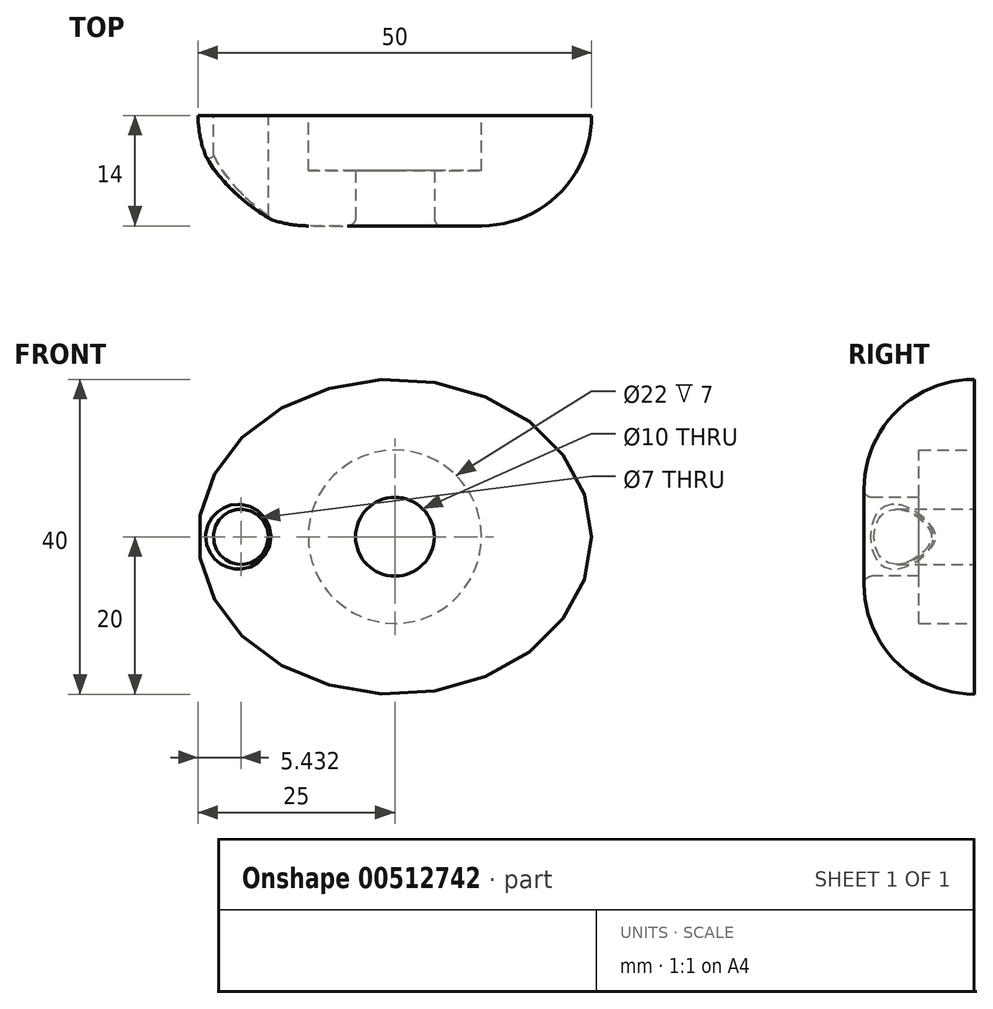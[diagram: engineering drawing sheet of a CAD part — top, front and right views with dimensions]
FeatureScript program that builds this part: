
annotation { "Feature Type Name" : "Feature", "Feature Type Description" : "" }
export const myFeature = defineFeature(function(context is Context, id is Id, definition is map)
    precondition{}
    {
        {
            var Q0;
            Q0=qCreatedBy(makeId("Front.planeOp"),FACE);
            var sketch = newSketch(context, id + "F0", { "sketchPlane" : qUnion([Q0])});
            skEllipse(sketch, "E0", {"center": v(0, 0) * mm, "majorRadius": 25 * mm, "minorRadius": 20 * mm, "majorAxis": v(1, 0)});
            skCircle(sketch, "E1", {"center": v(0, 0) * mm, "radius": 11 * mm});
            skSolve(sketch);
        }
        {
            var Q0;
            Q0=makeQuery(id+"F0.imprint","IMPRINT",FACE,{"disambiguationData":[TD([[makeQuery(id+"F0.imprint","IMPRINT",EDGE,{"derivedFrom":sQuery(id+"F0.wireOp",EDGE,"E0")}),1.0]])]});
            extrude(context, id + "F1", {"entities" : qUnion([Q0]), "depth" : 14 * mm});
        }
        {
            var Q0;
            Q0=makeQuery(id+"F1.opExtrude","CAP_FACE",FACE,{"disambiguationData":[OSD([sQuery(id+"F0.wireOp",EDGE,"E0"),sQuery(id+"F0.wireOp",EDGE,"E1")])],"isStart":false});
            var sketch = newSketch(context, id + "F2", { "sketchPlane" : qUnion([Q0])});
            skCircle(sketch, "E2", {"center": v(0, 0) * mm, "radius": 5 * mm});
            skSolve(sketch);
        }
        {
            var Q0;
            Q0=makeQuery(id+"F2.imprint","IMPRINT",FACE,{"disambiguationData":[TD([[makeQuery(id+"F2.imprint","IMPRINT",EDGE,{"derivedFrom":sQuery(id+"F2.wireOp",EDGE,"E2")}),-1.0]])]});
            extrude(context, id + "F3", {"entities" : qUnion([Q0]), "operationType" : NewBodyOperationType.ADD, "oppositeDirection" : true, "depth" : 7 * mm});
        }
        {
            var Q0;
            Q0=makeQuery(id+"F1.opExtrude","CAP_EDGE",EDGE,{"disambiguationData":[OSD([sQuery(id+"F0.wireOp",EDGE,"E0")])],"isStart":false});
            fillet(context, id + "F4", {"entities" : qUnion([Q0]), "radius" : 14 * mm, "allowEdgeOverflow" : false});
        }
        {
            var Q0;
            Q0=makeQuery(id+"F3.opExtrude","CAP_EDGE",EDGE,{"disambiguationData":[OSD([sQuery(id+"F2.wireOp",EDGE,"E2")])],"isStart":true});
            fillet(context, id + "F5", {"entities" : qUnion([Q0]), "radius" : 1 * mm, "tangentPropagation" : true, "allowEdgeOverflow" : false});
        }
        {
            var Q0;
            Q0=makeQuery(id+"F1.opExtrude","CAP_FACE",FACE,{"disambiguationData":[OSD([sQuery(id+"F0.wireOp",EDGE,"E0"),sQuery(id+"F0.wireOp",EDGE,"E1")])],"isStart":true});
            var sketch = newSketch(context, id + "F6", { "sketchPlane" : qUnion([Q0])});
            skCircle(sketch, "E3", {"center": v(19.57, 0) * mm, "radius": 3.5 * mm});
            skSolve(sketch);
        }
        {
            var Q0;
            Q0=makeQuery(id+"F6.imprint","IMPRINT",FACE,{"disambiguationData":[TD([[makeQuery(id+"F6.imprint","IMPRINT",EDGE,{"derivedFrom":sQuery(id+"F6.wireOp",EDGE,"E3")}),1.0]])]});
            extrude(context, id + "F7", {"entities" : qUnion([Q0]), "operationType" : NewBodyOperationType.REMOVE, "endBound" : BoundingType.THROUGH_ALL, "oppositeDirection" : true, "depth" : 25 * mm});
        }
        {
            var Q0;
            Q0=makeQuery(id+"F7.boolean.opBoolean","INTERSECT",EDGE,{"derivedFrom":[makeQuery(id+"F4.opFillet","BLEND_FACE",FACE,{"disambiguationData":[OSD([sQuery(id+"F0.wireOp",EDGE,"E0")])]}),makeQuery(id+"F7.opExtrude","SWEPT_FACE",FACE,{"disambiguationData":[OSD([sQuery(id+"F6.wireOp",EDGE,"E3")])]})]});
            fillet(context, id + "F8", {"entities" : qUnion([Q0]), "radius" : .5 * mm, "tangentPropagation" : true, "allowEdgeOverflow" : false});
        }
    });
